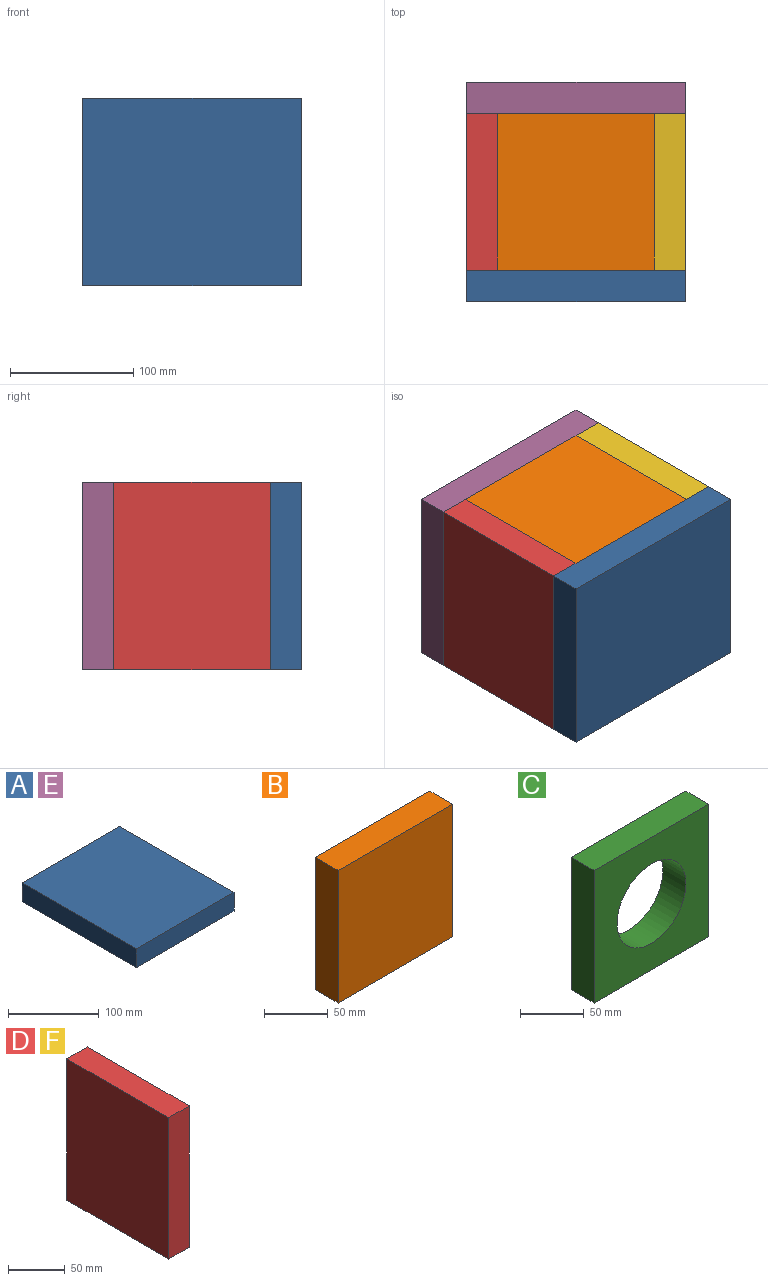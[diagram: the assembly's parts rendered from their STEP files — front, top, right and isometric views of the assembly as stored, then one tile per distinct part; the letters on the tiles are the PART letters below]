
ASSEMBLY  parts=6 mates=5
PART A: 6 faces, bbox 152.4x177.8x25.4 mm
  f0: plane 152.4x25.4mm, normal (0,1,0), area 3871mm2, adj f1,f3,f4,f5
  f1: plane 177.8x25.4mm, normal (-1,0,0), area 4516.1mm2, adj f0,f2,f4,f5
  f2: plane 152.4x25.4mm, normal (0,-1,0), area 3871mm2, adj f1,f3,f4,f5
  f3: plane 177.8x25.4mm, normal (1,0,0), area 4516.1mm2, adj f0,f2,f4,f5
  f4: plane 177.8x152.4mm, normal (0,0,1), area 27096.7mm2, adj f0,f1,f2,f3
  f5: plane 177.8x152.4mm, normal (0,0,-1), area 27096.7mm2, adj f0,f1,f2,f3
PART B: 6 faces, bbox 127x25.4x127 mm
  f0: plane 127x25.4mm, normal (0,0,1), area 3225.8mm2, adj f1,f3,f4,f5
  f1: plane 127x25.4mm, normal (-1,0,0), area 3225.8mm2, adj f0,f2,f4,f5
  f2: plane 127x25.4mm, normal (0,0,-1), area 3225.8mm2, adj f1,f3,f4,f5
  f3: plane 127x25.4mm, normal (1,0,0), area 3225.8mm2, adj f0,f2,f4,f5
  f4: plane 127x127mm, normal (0,-1,0), area 16129mm2, adj f0,f1,f2,f3
  f5: plane 127x127mm, normal (0,1,0), area 16129mm2, adj f0,f1,f2,f3
PART C: 7 faces, bbox 127x25.4x127 mm
  f0: plane 127x25.4mm, normal (0,0,1), area 3225.8mm2, adj f1,f3,f4,f5
  f1: plane 127x25.4mm, normal (-1,0,0), area 3225.8mm2, adj f0,f2,f4,f5
  f2: plane 127x25.4mm, normal (0,0,-1), area 3225.8mm2, adj f1,f3,f4,f5
  f3: plane 127x25.4mm, normal (1,0,0), area 3225.8mm2, adj f0,f2,f4,f5
  f4: plane 127x127mm, normal (0,-1,0), area 11568.6mm2, adj f0,f1,f2,f3,f6
  f5: plane 127x127mm, normal (0,1,0), area 11568.6mm2, adj f0,f1,f2,f3,f6
  f6: cylinder r=38.1mm len=76.2mm, axis (0,-1,0), area 6080.5mm2, adj f4,f5
PART D: 6 faces, bbox 25.4x127x152.4 mm
  f0: plane 127x25.4mm, normal (0,0,1), area 3225.8mm2, adj f1,f3,f4,f5
  f1: plane 152.4x25.4mm, normal (0,-1,0), area 3871mm2, adj f0,f2,f4,f5
  f2: plane 127x25.4mm, normal (0,0,-1), area 3225.8mm2, adj f1,f3,f4,f5
  f3: plane 152.4x25.4mm, normal (0,1,0), area 3871mm2, adj f0,f2,f4,f5
  f4: plane 152.4x127mm, normal (1,0,0), area 19354.8mm2, adj f0,f1,f2,f3
  f5: plane 152.4x127mm, normal (-1,0,0), area 19354.8mm2, adj f0,f1,f2,f3
PART E: same geometry as A
PART F: same geometry as D
PLACE A rot(axis=(-0.58,-0.58,-0.58),120deg) t=(139.1,-210.77,174.52)mm
PLACE B rot(axis=(-1,0,0),90deg) t=(150,-132.4,232.48)mm
PLACE C rot(axis=(1,0,0),90deg) t=(144.14,-84.51,130.88)mm
PLACE D rot(axis=(0,0,1),180deg) t=(89.59,-142.18,185.9)mm
PLACE E rot(axis=(0.58,0.58,-0.58),120deg) t=(139.1,-32.97,188.83)mm
PLACE F t=(216.59,-101.56,185.9)mm
MATE fastened D.f5 <-> C.f1  axis (1,0,0) through (89.59,-121.87,105.48)mm
MATE fastened E.f4 <-> F.f3  axis (0,-1,0) through (241.99,-58.37,181.68)mm
MATE fastened C.f3 <-> F.f5  axis (1,0,0) through (216.59,-121.87,105.48)mm
MATE fastened A.f4 <-> C.f0  axis (0,1,0) through (153.09,-185.37,105.48)mm
MATE fastened B.f1 <-> D.f5  axis (-1,0,0) through (89.59,-121.87,257.88)mm
